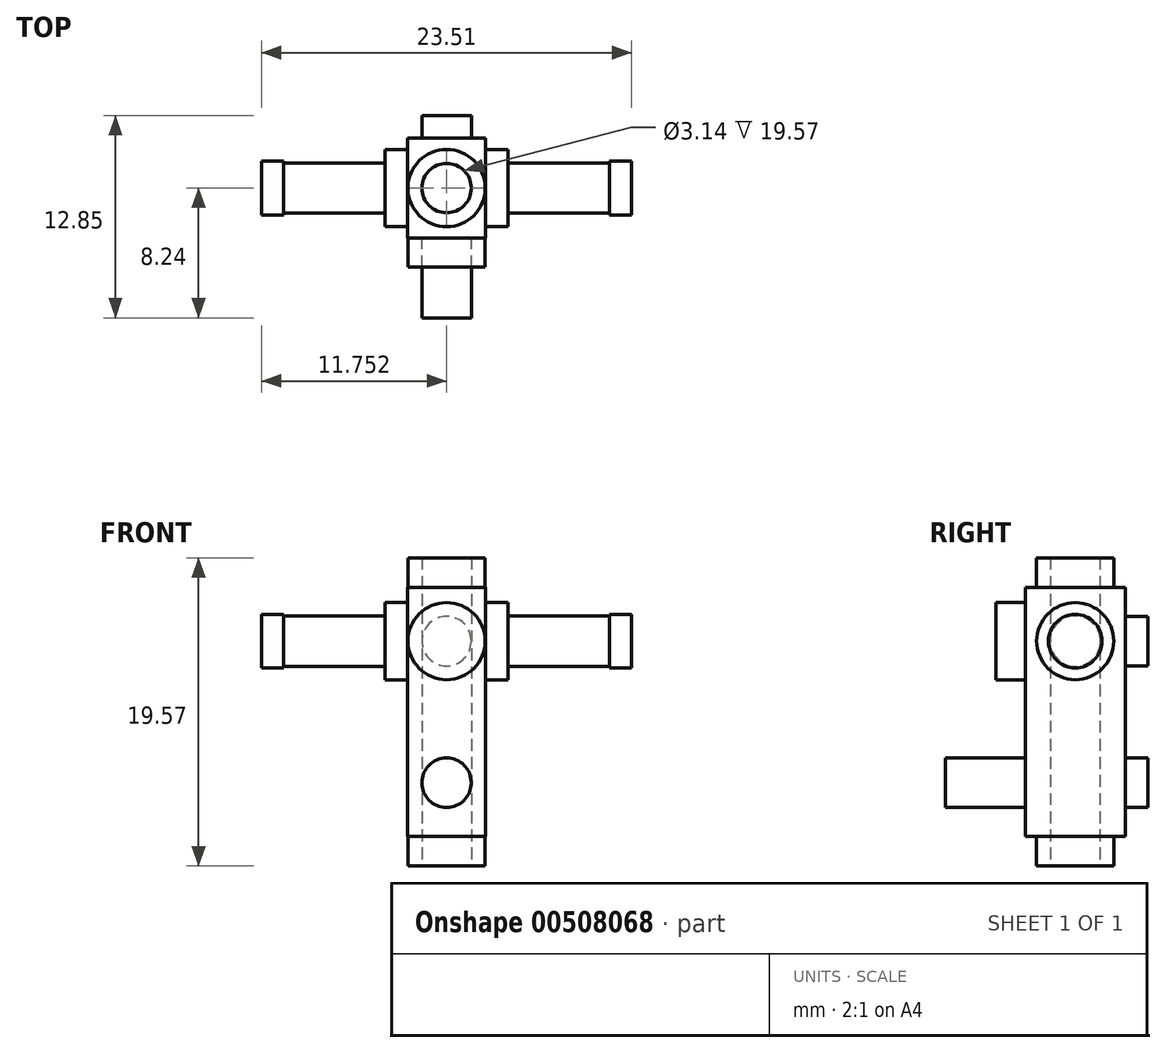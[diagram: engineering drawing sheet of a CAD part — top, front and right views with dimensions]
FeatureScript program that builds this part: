
annotation { "Feature Type Name" : "Feature", "Feature Type Description" : "" }
export const myFeature = defineFeature(function(context is Context, id is Id, definition is map)
    precondition{}
    {
        {
            var Q0;
            Q0=qCreatedBy(makeId("Front.planeOp"),FACE);
            var sketch = newSketch(context, id + "F0", { "sketchPlane" : qUnion([Q0])});
            skLineSegment(sketch, "E0.bottom", {"start": v(-30.43, 19.36) * mm, "end": v(-25.47, 19.36) * mm});
            skLineSegment(sketch, "E0.top", {"start": v(-30.43, 3.53) * mm, "end": v(-25.47, 3.53) * mm});
            skLineSegment(sketch, "E0.left", {"start": v(-30.43, 19.36) * mm, "end": v(-30.43, 3.53) * mm});
            skLineSegment(sketch, "E0.right", {"start": v(-25.47, 19.36) * mm, "end": v(-25.47, 3.53) * mm});
            skSolve(sketch);
        }
        {
            var Q0;
            Q0 = qSketchRegion(id + "F0", true);
            extrude(context, id + "F1", {"entities" : qUnion([Q0]), "depth" : 6.36 * mm, "offsetDistance" : 25 * mm});
        }
        {
            var Q0;
            Q0=makeQuery(id+"F1.opExtrude","CAP_FACE",FACE,{"disambiguationData":[OSD([sQuery(id+"F0.wireOp",EDGE,"E0.bottom"),sQuery(id+"F0.wireOp",EDGE,"E0.top"),sQuery(id+"F0.wireOp",EDGE,"E0.left"),sQuery(id+"F0.wireOp",EDGE,"E0.right")])],"isStart":false});
            var sketch = newSketch(context, id + "F2", { "sketchPlane" : qUnion([Q0])});
            skCircle(sketch, "E1", {"center": v(-27.95, 15.94) * mm, "radius": 2.45 * mm});
            skPoint(sketch, "E1.centerSnap0", {"position": v(-27.95, 19.36) * mm});
            skSolve(sketch);
        }
        {
            var Q0;
            Q0 = qSketchRegion(id + "F2", true);
            extrude(context, id + "F3", {"entities" : qUnion([Q0]), "operationType" : NewBodyOperationType.ADD, "depth" : 1.84 * mm, "offsetDistance" : 25 * mm});
        }
        {
            var Q0;
            Q0=makeQuery(id+"F1.opExtrude","SWEPT_FACE",FACE,{"disambiguationData":[OSD([sQuery(id+"F0.wireOp",EDGE,"E0.bottom")])]});
            var sketch = newSketch(context, id + "F4", { "sketchPlane" : qUnion([Q0])});
            skCircle(sketch, "E2", {"center": v(-27.95, -3.18) * mm, "radius": 2.45 * mm});
            skPoint(sketch, "E2.centerSnap0", {"position": v(-27.95, 0) * mm});
            skPoint(sketch, "E2.centerSnap1", {"position": v(-25.47, -3.18) * mm});
            skSolve(sketch);
        }
        {
            var Q0;
            Q0 = qSketchRegion(id + "F4", true);
            extrude(context, id + "F5", {"entities" : qUnion([Q0]), "operationType" : NewBodyOperationType.ADD, "depth" : 1.87 * mm, "offsetDistance" : 25 * mm});
        }
        {
            var Q0;
            Q0=makeQuery(id+"F1.opExtrude","SWEPT_FACE",FACE,{"disambiguationData":[OSD([sQuery(id+"F0.wireOp",EDGE,"E0.top")])]});
            var sketch = newSketch(context, id + "F6", { "sketchPlane" : qUnion([Q0])});
            skCircle(sketch, "E3", {"center": v(-27.95, 3.18) * mm, "radius": 2.45 * mm});
            skPoint(sketch, "E3.centerSnap0", {"position": v(-30.43, 3.18) * mm});
            skPoint(sketch, "E3.centerSnap1", {"position": v(-27.95, 0) * mm});
            skSolve(sketch);
        }
        {
            var Q0;
            Q0 = qSketchRegion(id + "F6", true);
            extrude(context, id + "F7", {"entities" : qUnion([Q0]), "operationType" : NewBodyOperationType.ADD, "depth" : 1.87 * mm, "offsetDistance" : 25 * mm});
        }
        {
            var Q0;
            Q0=makeQuery(id+"F7.opExtrude","CAP_FACE",FACE,{"disambiguationData":[OSD([sQuery(id+"F6.wireOp",EDGE,"E3")])],"isStart":false});
            var sketch = newSketch(context, id + "F8", { "sketchPlane" : qUnion([Q0])});
            skCircle(sketch, "E4", {"center": v(-27.95, 3.18) * mm, "radius": 1.57 * mm});
            skSolve(sketch);
        }
        {
            var Q0;
            Q0=sQuery(id+"F8.wireOp",VERTEX,"E4.center");
            var Q1;
            Q1=makeQuery(id+"F1.opExtrude","SWEPT_BODY",BODY,{"disambiguationData":[OSD([sQuery(id+"F0.wireOp",EDGE,"E0.bottom"),sQuery(id+"F0.wireOp",EDGE,"E0.top"),sQuery(id+"F0.wireOp",EDGE,"E0.left"),sQuery(id+"F0.wireOp",EDGE,"E0.right")])]});
            hole(context, id + "F9", {"style" : HoleStyle.SIMPLE, "endStyle" : HoleEndStyle.THROUGH, "holeDiameter" : 3.14 * mm, "isTappedThrough" : true, "tappedDepth" : 12 * mm, "tapClearance" : 3, "locations" : qUnion([Q0]), "scope" : qUnion([Q1])});
        }
        {
            var Q0;
            Q0=makeQuery(id+"F1.opExtrude","SWEPT_FACE",FACE,{"disambiguationData":[OSD([sQuery(id+"F0.wireOp",EDGE,"E0.right")])]});
            var sketch = newSketch(context, id + "F10", { "sketchPlane" : qUnion([Q0])});
            skCircle(sketch, "E5", {"center": v(-3.18, 15.94) * mm, "radius": 2.45 * mm});
            skPoint(sketch, "E5.centerSnap0", {"position": v(-3.18, 19.36) * mm});
            skSolve(sketch);
        }
        {
            var Q0;
            Q0 = qSketchRegion(id + "F10", true);
            extrude(context, id + "F11", {"entities" : qUnion([Q0]), "operationType" : NewBodyOperationType.ADD, "depth" : 1.43 * mm, "offsetDistance" : 25 * mm});
        }
        {
            var Q0;
            Q0=makeQuery(id+"F1.opExtrude","SWEPT_FACE",FACE,{"disambiguationData":[OSD([sQuery(id+"F0.wireOp",EDGE,"E0.left")])]});
            var sketch = newSketch(context, id + "F12", { "sketchPlane" : qUnion([Q0])});
            skCircle(sketch, "E6", {"center": v(3.18, 15.94) * mm, "radius": 2.45 * mm});
            skPoint(sketch, "E6.centerSnap0", {"position": v(3.18, 19.36) * mm});
            skSolve(sketch);
        }
        {
            var Q0;
            Q0=makeQuery(id+"F12.imprint","IMPRINT",FACE,{"disambiguationData":[TD([[makeQuery(id+"F12.imprint","IMPRINT",EDGE,{"derivedFrom":sQuery(id+"F12.wireOp",EDGE,"E6")}),1.0]])]});
            extrude(context, id + "F13", {"entities" : qUnion([Q0]), "operationType" : NewBodyOperationType.ADD, "depth" : 1.43 * mm, "offsetDistance" : 25 * mm});
        }
        {
            var Q0;
            Q0=makeQuery(id+"F1.opExtrude","CAP_FACE",FACE,{"disambiguationData":[OSD([sQuery(id+"F0.wireOp",EDGE,"E0.bottom"),sQuery(id+"F0.wireOp",EDGE,"E0.top"),sQuery(id+"F0.wireOp",EDGE,"E0.left"),sQuery(id+"F0.wireOp",EDGE,"E0.right")])],"isStart":false});
            var sketch = newSketch(context, id + "F14", { "sketchPlane" : qUnion([Q0])});
            skCircle(sketch, "E7", {"center": v(-27.95, 6.95) * mm, "radius": 1.57 * mm});
            skPoint(sketch, "E7.centerSnap0", {"position": v(-27.95, 3.53) * mm});
            skSolve(sketch);
        }
        {
            var Q0;
            Q0 = qSketchRegion(id + "F14", true);
            extrude(context, id + "F15", {"entities" : qUnion([Q0]), "operationType" : NewBodyOperationType.ADD, "depth" : 5.06 * mm, "offsetDistance" : 25 * mm});
        }
        {
            var Q0;
            Q0=makeQuery(id+"F1.opExtrude","CAP_FACE",FACE,{"disambiguationData":[OSD([sQuery(id+"F0.wireOp",EDGE,"E0.bottom"),sQuery(id+"F0.wireOp",EDGE,"E0.top"),sQuery(id+"F0.wireOp",EDGE,"E0.left"),sQuery(id+"F0.wireOp",EDGE,"E0.right")])],"isStart":true});
            var sketch = newSketch(context, id + "F16", { "sketchPlane" : qUnion([Q0])});
            skCircle(sketch, "E8", {"center": v(27.95, 15.94) * mm, "radius": 1.57 * mm});
            skPoint(sketch, "E8.centerSnap0", {"position": v(27.95, 19.36) * mm});
            skLineSegment(sketch, "E9", {"start": v(25.47, 11.45) * mm, "end": v(30.43, 11.45) * mm});
            skCircle(sketch, "E10.MirrorC", {"center": v(27.95, 6.95) * mm, "radius": 1.57 * mm});
            skSolve(sketch);
        }
        {
            var Q0;
            Q0 = qSketchRegion(id + "F16", true);
            extrude(context, id + "F17", {"entities" : qUnion([Q0]), "operationType" : NewBodyOperationType.ADD, "depth" : 1.43 * mm, "offsetDistance" : 25 * mm});
        }
        {
            var Q0;
            Q0=makeQuery(id+"F13.opExtrude","CAP_FACE",FACE,{"disambiguationData":[OSD([sQuery(id+"F12.wireOp",EDGE,"E6")])],"isStart":false});
            var sketch = newSketch(context, id + "F18", { "sketchPlane" : qUnion([Q0])});
            skCircle(sketch, "E11", {"center": v(3.18, 15.94) * mm, "radius": 1.6 * mm});
            skSolve(sketch);
        }
        {
            var Q0;
            Q0 = qSketchRegion(id + "F18", true);
            extrude(context, id + "F19", {"entities" : qUnion([Q0]), "operationType" : NewBodyOperationType.ADD, "depth" : 6.43 * mm, "offsetDistance" : 25 * mm});
        }
        {
            var Q0;
            Q0=makeQuery(id+"F19.opExtrude","CAP_FACE",FACE,{"disambiguationData":[OSD([sQuery(id+"F18.wireOp",EDGE,"E11")])],"isStart":false});
            var sketch = newSketch(context, id + "F20", { "sketchPlane" : qUnion([Q0])});
            skCircle(sketch, "E12", {"center": v(3.18, 15.94) * mm, "radius": 1.7 * mm});
            skSolve(sketch);
        }
        {
            var Q0;
            Q0 = qSketchRegion(id + "F20", true);
            extrude(context, id + "F21", {"entities" : qUnion([Q0]), "operationType" : NewBodyOperationType.ADD, "depth" : 1.41 * mm, "offsetDistance" : 25 * mm});
        }
        {
            var Q0;
            Q0=makeQuery(id+"F11.opExtrude","CAP_FACE",FACE,{"disambiguationData":[OSD([sQuery(id+"F10.wireOp",EDGE,"E5")])],"isStart":false});
            var sketch = newSketch(context, id + "F22", { "sketchPlane" : qUnion([Q0])});
            skCircle(sketch, "E13", {"center": v(-3.18, 15.94) * mm, "radius": 1.6 * mm});
            skSolve(sketch);
        }
        {
            var Q0;
            Q0 = qSketchRegion(id + "F22", true);
            extrude(context, id + "F23", {"entities" : qUnion([Q0]), "operationType" : NewBodyOperationType.ADD, "depth" : 6.43 * mm, "offsetDistance" : 25 * mm});
        }
        {
            var Q0;
            Q0=makeQuery(id+"F23.opExtrude","CAP_FACE",FACE,{"disambiguationData":[OSD([sQuery(id+"F22.wireOp",EDGE,"E13")])],"isStart":false});
            var sketch = newSketch(context, id + "F24", { "sketchPlane" : qUnion([Q0])});
            skCircle(sketch, "E14", {"center": v(-3.18, 15.94) * mm, "radius": 1.7 * mm});
            skSolve(sketch);
        }
        {
            var Q0;
            Q0 = qSketchRegion(id + "F24", true);
            extrude(context, id + "F25", {"entities" : qUnion([Q0]), "operationType" : NewBodyOperationType.ADD, "depth" : 1.41 * mm, "offsetDistance" : 25 * mm});
        }
    });
